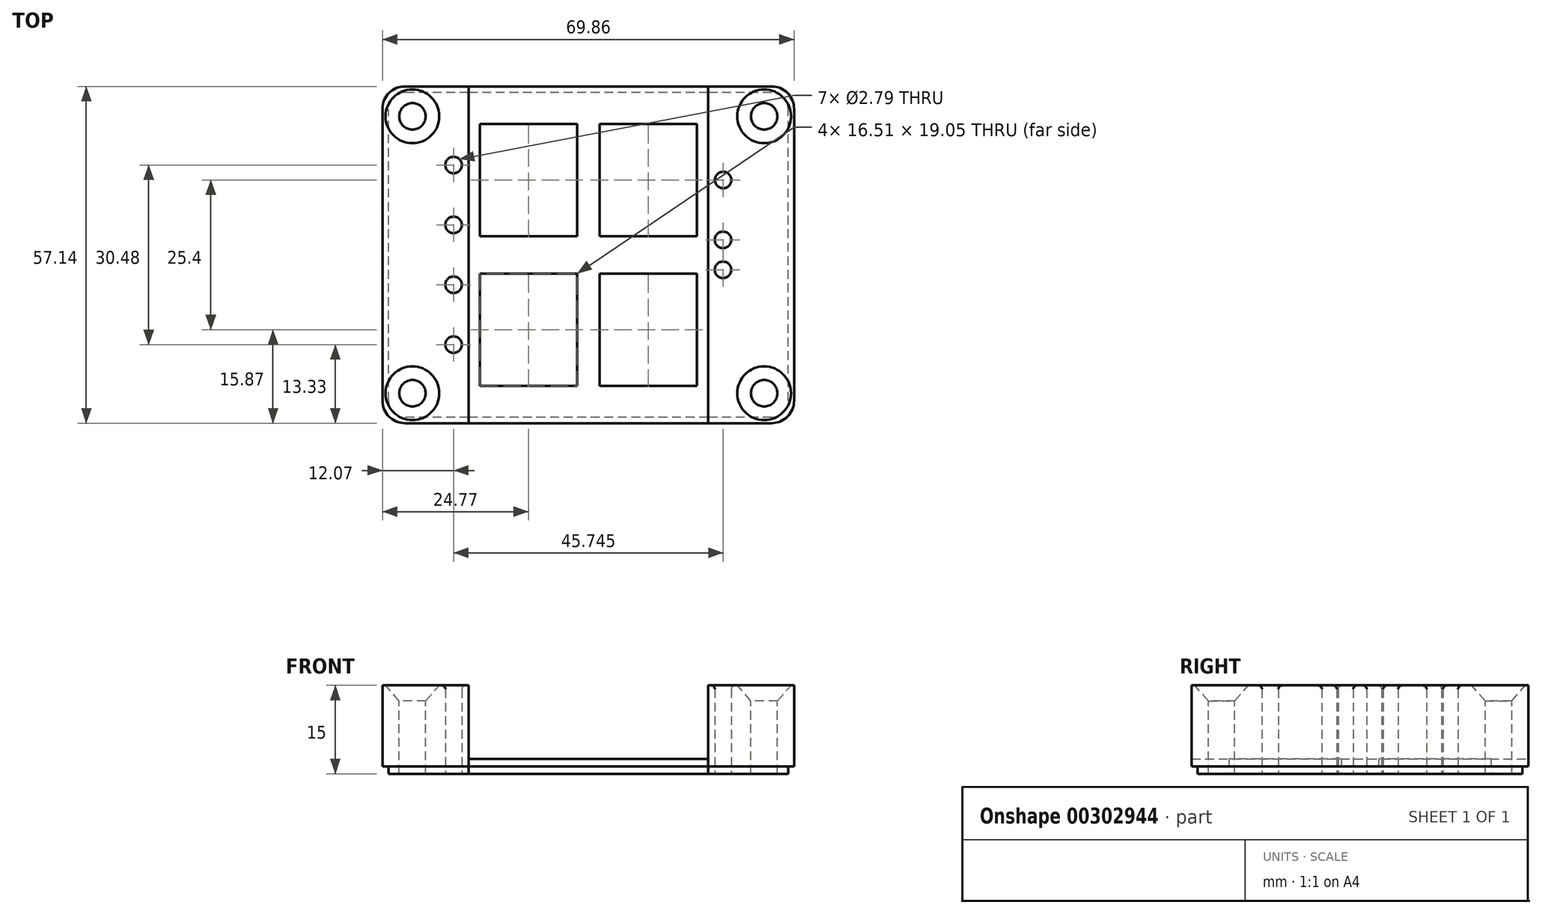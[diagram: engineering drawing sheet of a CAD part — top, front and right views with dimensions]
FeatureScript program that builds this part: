
annotation { "Feature Type Name" : "Feature", "Feature Type Description" : "" }
export const myFeature = defineFeature(function(context is Context, id is Id, definition is map)
    precondition{}
    {
        {
            var Q0;
            Q0=qCreatedBy(makeId("Top.planeOp"),FACE);
            var sketch = newSketch(context, id + "F0", { "sketchPlane" : qUnion([Q0])});
            skLineSegment(sketch, "E0.bottom", {"start": v(34.93, -28.58) * mm, "end": v(-34.93, -28.58) * mm});
            skLineSegment(sketch, "E0.top", {"start": v(34.93, 28.58) * mm, "end": v(-34.93, 28.57) * mm});
            skLineSegment(sketch, "E0.left", {"start": v(34.93, -28.58) * mm, "end": v(34.93, 28.58) * mm});
            skLineSegment(sketch, "E0.right", {"start": v(-34.93, -28.58) * mm, "end": v(-34.93, 28.58) * mm});
            skPoint(sketch, "E0.middle", {"position": v(0, 0) * mm});
            skLineSegment(sketch, "E1.bottom", {"start": v(20.32, -25.65) * mm, "end": v(-20.32, -25.65) * mm});
            skLineSegment(sketch, "E1.top", {"start": v(20.32, 25.65) * mm, "end": v(-20.32, 25.65) * mm});
            skLineSegment(sketch, "E1.left", {"start": v(20.32, -25.65) * mm, "end": v(20.32, 25.65) * mm});
            skLineSegment(sketch, "E1.right", {"start": v(-20.32, -25.65) * mm, "end": v(-20.32, 25.65) * mm});
            skCircle(sketch, "E2", {"center": v(-22.86, -15.24) * mm, "radius": 1.4 * mm});
            skCircle(sketch, "E3", {"center": v(-22.86, -5.08) * mm, "radius": 1.4 * mm});
            skCircle(sketch, "E4", {"center": v(-22.86, 5.08) * mm, "radius": 1.4 * mm});
            skCircle(sketch, "E5", {"center": v(-22.86, 15.24) * mm, "radius": 1.4 * mm});
            skCircle(sketch, "E6", {"center": v(22.86, -2.54) * mm, "radius": 1.4 * mm});
            skCircle(sketch, "E7", {"center": v(22.86, 2.54) * mm, "radius": 1.4 * mm});
            skCircle(sketch, "E8", {"center": v(22.88, 12.7) * mm, "radius": 1.4 * mm});
            skLineSegment(sketch, "E9", {"start": v(-20.32, -25.65) * mm, "end": v(-20.32, -28.58) * mm});
            skLineSegment(sketch, "E10", {"start": v(20.32, -25.65) * mm, "end": v(20.32, -28.58) * mm});
            skLineSegment(sketch, "E11", {"start": v(20.32, 25.65) * mm, "end": v(20.32, 28.58) * mm});
            skLineSegment(sketch, "E12", {"start": v(-20.32, 25.65) * mm, "end": v(-20.32, 28.57) * mm});
            skLineSegment(sketch, "E13.bottom", {"start": v(1.9, -3.18) * mm, "end": v(18.41, -3.18) * mm});
            skLineSegment(sketch, "E13.top", {"start": v(1.9, -22.23) * mm, "end": v(18.41, -22.23) * mm});
            skLineSegment(sketch, "E13.left", {"start": v(1.9, -3.18) * mm, "end": v(1.9, -22.23) * mm});
            skLineSegment(sketch, "E13.right", {"start": v(18.41, -3.18) * mm, "end": v(18.41, -22.23) * mm});
            skPoint(sketch, "E13.middle", {"position": v(10.16, -12.7) * mm});
            skLineSegment(sketch, "E14.0.1.0", {"start": v(18.41, 22.22) * mm, "end": v(18.41, 3.17) * mm});
            skLineSegment(sketch, "E14.0.1.1", {"start": v(1.9, 22.22) * mm, "end": v(1.9, 3.17) * mm});
            skLineSegment(sketch, "E14.0.1.2", {"start": v(1.9, 3.17) * mm, "end": v(18.41, 3.17) * mm});
            skLineSegment(sketch, "E14.0.1.3", {"start": v(1.9, 22.22) * mm, "end": v(18.41, 22.22) * mm});
            skLineSegment(sketch, "E14.1.0.0", {"start": v(-1.9, -3.18) * mm, "end": v(-1.9, -22.23) * mm});
            skLineSegment(sketch, "E14.1.0.1", {"start": v(-18.42, -3.18) * mm, "end": v(-18.42, -22.23) * mm});
            skLineSegment(sketch, "E14.1.0.2", {"start": v(-18.42, -22.23) * mm, "end": v(-1.9, -22.23) * mm});
            skLineSegment(sketch, "E14.1.0.3", {"start": v(-18.42, -3.18) * mm, "end": v(-1.9, -3.18) * mm});
            skLineSegment(sketch, "E14.1.1.0", {"start": v(-1.9, 22.22) * mm, "end": v(-1.9, 3.17) * mm});
            skLineSegment(sketch, "E14.1.1.1", {"start": v(-18.42, 22.22) * mm, "end": v(-18.42, 3.17) * mm});
            skLineSegment(sketch, "E14.1.1.2", {"start": v(-18.42, 3.17) * mm, "end": v(-1.9, 3.17) * mm});
            skLineSegment(sketch, "E14.1.1.3", {"start": v(-18.42, 22.22) * mm, "end": v(-1.9, 22.22) * mm});
            skLineSegment(sketch, "E14.direction1", {"start": v(1.9, -3.18) * mm, "end": v(-18.42, -3.18) * mm, "construction": true});
            skLineSegment(sketch, "E14.direction2", {"start": v(1.9, -3.18) * mm, "end": v(1.9, 22.22) * mm, "construction": true});
            skSolve(sketch);
        }
        {
            var Q0;
            {var subQ0=sQuery(id+"F0.wireOp",EDGE,"E0.right");Q0=makeQuery(id+"F0.imprint","IMPRINT",FACE,{"disambiguationData":[TD([[makeQuery(id+"F0.imprint","IMPRINT",EDGE,{"derivedFrom":subQ0}),-1.0]])]});}
            var Q1;
            {var subQ1=sQuery(id+"F0.wireOp",EDGE,"E0.left");Q1=makeQuery(id+"F0.imprint","IMPRINT",FACE,{"disambiguationData":[TD([[makeQuery(id+"F0.imprint","IMPRINT",EDGE,{"derivedFrom":subQ1}),1.0]])]});}
            var Q2;
            Q2=makeQuery(id+"F0.imprint","IMPRINT",FACE,{"disambiguationData":[TD([[makeQuery(id+"F0.imprint","IMPRINT",EDGE,{"derivedFrom":sQuery(id+"F0.wireOp",EDGE,"b5f2c712-6844-453f-bde0-8a3109862096")}),1.0]])]});
            var Q3;
            Q3=makeQuery(id+"F0.imprint","IMPRINT",FACE,{"disambiguationData":[TD([[makeQuery(id+"F0.imprint","IMPRINT",EDGE,{"derivedFrom":sQuery(id+"F0.wireOp",EDGE,"b4171f42-6c98-4037-92a8-ff7a6a93fe7b")}),1.0]])]});
            var Q4;
            Q4=makeQuery(id+"F0.imprint","IMPRINT",FACE,{"disambiguationData":[TD([[makeQuery(id+"F0.imprint","IMPRINT",EDGE,{"derivedFrom":sQuery(id+"F0.wireOp",EDGE,"d604e2b2-1cbf-4e45-8d46-6f62e81bd806")}),1.0]])]});
            var Q5;
            Q5=makeQuery(id+"F0.imprint","IMPRINT",FACE,{"disambiguationData":[TD([[makeQuery(id+"F0.imprint","IMPRINT",EDGE,{"derivedFrom":sQuery(id+"F0.wireOp",EDGE,"b88a7e70-b00d-4436-bc84-b71cc6af67d6")}),1.0]])]});
            extrude(context, id + "F1", {"entities" : qUnion([Q0, Q1, Q2, Q3, Q4, Q5]), "depth" : 15 * mm});
        }
        {
            var Q0;
            Q0=makeQuery(id+"F0.imprint","IMPRINT",FACE,{"disambiguationData":[TD([[makeQuery(id+"F0.imprint","IMPRINT",EDGE,{"derivedFrom":sQuery(id+"F0.wireOp",EDGE,"E1.bottom")}),-1.0]])]});
            var Q1;
            Q1=makeQuery(id+"F0.imprint","IMPRINT",FACE,{"disambiguationData":[TD([[makeQuery(id+"F0.imprint","IMPRINT",EDGE,{"derivedFrom":sQuery(id+"F0.wireOp",EDGE,"E1.bottom")}),1.0]])]});
            var Q2;
            Q2=makeQuery(id+"F0.imprint","IMPRINT",FACE,{"disambiguationData":[TD([[makeQuery(id+"F0.imprint","IMPRINT",EDGE,{"derivedFrom":sQuery(id+"F0.wireOp",EDGE,"E1.top")}),-1.0]])]});
            extrude(context, id + "F2", {"entities" : qUnion([Q0, Q1, Q2]), "depth" : 2.54 * mm});
        }
        {
            var Q0;
            Q0=makeQuery(id+"F1.opExtrude","SWEPT_EDGE",EDGE,{"disambiguationData":[OSD([sQuery(id+"F0.wireOp",EDGE,"E0.bottom"),sQuery(id+"F0.wireOp",EDGE,"E0.left")])]});
            var Q1;
            Q1=makeQuery(id+"F1.opExtrude","SWEPT_EDGE",EDGE,{"disambiguationData":[OSD([sQuery(id+"F0.wireOp",EDGE,"E0.bottom"),sQuery(id+"F0.wireOp",EDGE,"E0.right")])]});
            var Q2;
            Q2=makeQuery(id+"F1.opExtrude","SWEPT_EDGE",EDGE,{"disambiguationData":[OSD([sQuery(id+"F0.wireOp",EDGE,"E0.top"),sQuery(id+"F0.wireOp",EDGE,"E0.left")])]});
            var Q3;
            Q3=makeQuery(id+"F1.opExtrude","SWEPT_EDGE",EDGE,{"disambiguationData":[OSD([sQuery(id+"F0.wireOp",EDGE,"E0.top"),sQuery(id+"F0.wireOp",EDGE,"E0.right")])]});
            fillet(context, id + "F3", {"entities" : qUnion([Q0, Q1, Q2, Q3]), "radius" : 3.8 * mm, "tangentPropagation" : true, "allowEdgeOverflow" : false});
        }
        {
            var Q0;
            Q0=makeQuery(id+"F1.opExtrude","CAP_EDGE",EDGE,{"disambiguationData":[OSD([sQuery(id+"F0.wireOp",EDGE,"E2")])],"isStart":false});
            var Q1;
            Q1=makeQuery(id+"F1.opExtrude","CAP_EDGE",EDGE,{"disambiguationData":[OSD([sQuery(id+"F0.wireOp",EDGE,"E3")])],"isStart":false});
            var Q2;
            Q2=makeQuery(id+"F1.opExtrude","CAP_EDGE",EDGE,{"disambiguationData":[OSD([sQuery(id+"F0.wireOp",EDGE,"E4")])],"isStart":false});
            var Q3;
            Q3=makeQuery(id+"F1.opExtrude","CAP_EDGE",EDGE,{"disambiguationData":[OSD([sQuery(id+"F0.wireOp",EDGE,"E5")])],"isStart":false});
            var Q4;
            Q4=makeQuery(id+"F1.opExtrude","CAP_EDGE",EDGE,{"disambiguationData":[OSD([sQuery(id+"F0.wireOp",EDGE,"E8")])],"isStart":false});
            var Q5;
            Q5=makeQuery(id+"F1.opExtrude","CAP_EDGE",EDGE,{"disambiguationData":[OSD([sQuery(id+"F0.wireOp",EDGE,"E7")])],"isStart":false});
            var Q6;
            Q6=makeQuery(id+"F1.opExtrude","CAP_EDGE",EDGE,{"disambiguationData":[OSD([sQuery(id+"F0.wireOp",EDGE,"E6")])],"isStart":false});
            fillet(context, id + "F4", {"entities" : qUnion([Q0, Q1, Q2, Q3, Q4, Q5, Q6]), "radius" : 0.64 * mm, "tangentPropagation" : true, "allowEdgeOverflow" : false});
        }
        {
            var Q0;
            Q0=qCreatedBy(makeId("Top.planeOp"),FACE);
            cPlane(context, id + "F5", {"entities" : qUnion([Q0]), "cplaneType" : CPlaneType.OFFSET, "offset" : 15 * mm, "width" : 152.4 * mm, "height" : 152.4 * mm});
        }
        {
            var Q0;
            Q0=qCreatedBy(id+"F5.planeOp",FACE);
            var sketch = newSketch(context, id + "F6", { "sketchPlane" : qUnion([Q0])});
            skPoint(sketch, "E15", {"position": v(29.85, -23.5) * mm});
            skPoint(sketch, "E16", {"position": v(29.85, 23.5) * mm});
            skPoint(sketch, "E17", {"position": v(-29.85, 23.5) * mm});
            skPoint(sketch, "E18", {"position": v(-29.85, -23.5) * mm});
            skSolve(sketch);
        }
        {
            var Q0;
            Q0=sQuery(id+"F6.wireOp",VERTEX,"E15");
            var Q1;
            Q1=sQuery(id+"F6.wireOp",VERTEX,"E16");
            var Q2;
            Q2=sQuery(id+"F6.wireOp",VERTEX,"E17");
            var Q3;
            Q3=sQuery(id+"F6.wireOp",VERTEX,"E18");
            var Q4;
            Q4=makeQuery(id+"F1.opExtrude","SWEPT_BODY",BODY,{"disambiguationData":[OSD([sQuery(id+"F0.wireOp",EDGE,"E0.bottom"),sQuery(id+"F0.wireOp",EDGE,"E0.top"),sQuery(id+"F0.wireOp",EDGE,"E0.left"),sQuery(id+"F0.wireOp",EDGE,"E1.left"),sQuery(id+"F0.wireOp",EDGE,"E6"),sQuery(id+"F0.wireOp",EDGE,"E7"),sQuery(id+"F0.wireOp",EDGE,"E8"),sQuery(id+"F0.wireOp",EDGE,"E10"),sQuery(id+"F0.wireOp",EDGE,"E11")])]});
            var Q5;
            Q5=makeQuery(id+"F1.opExtrude","SWEPT_BODY",BODY,{"disambiguationData":[OSD([sQuery(id+"F0.wireOp",EDGE,"E0.bottom"),sQuery(id+"F0.wireOp",EDGE,"E0.top"),sQuery(id+"F0.wireOp",EDGE,"E0.right"),sQuery(id+"F0.wireOp",EDGE,"E1.right"),sQuery(id+"F0.wireOp",EDGE,"E2"),sQuery(id+"F0.wireOp",EDGE,"E3"),sQuery(id+"F0.wireOp",EDGE,"E4"),sQuery(id+"F0.wireOp",EDGE,"E5"),sQuery(id+"F0.wireOp",EDGE,"E9"),sQuery(id+"F0.wireOp",EDGE,"E12")])]});
            hole(context, id + "F7", {"style" : HoleStyle.C_SINK, "endStyle" : HoleEndStyle.THROUGH, "standardTappedOrClearance" : lookupTablePath({ "standard" : "ANSI", "fit" : "Normal (ASME)", "size" : "#8", "type" : "Clearance" }), "standardBlindInLast" : lookupTablePath({ "fit" : "Free", "standard" : "ANSI", "size" : "#8", "type" : "Clearance" }), "holeDiameter" : 4.5 * mm, "cSinkDiameter" : 9.12 * mm, "cSinkAngle" : 82 * degree, "tappedDepth" : 12.7 * mm, "tapClearance" : 3, "locations" : qUnion([Q0, Q1, Q2, Q3]), "scope" : qUnion([Q4, Q5])});
        }
        {
            var Q0;
            {var subQ0=sQuery(id+"F0.wireOp",EDGE,"E0.left");Q0=makeQuery(id+"F0.imprint","IMPRINT",FACE,{"disambiguationData":[TD([[makeQuery(id+"F0.imprint","IMPRINT",EDGE,{"derivedFrom":subQ0}),1.0]])]});}
            var sketch = newSketch(context, id + "F8", { "sketchPlane" : qUnion([Q0])});
            skLineSegment(sketch, "E19.0", {"start": v(31.12, 27.56) * mm, "end": v(20.32, 27.56) * mm});
            skLineSegment(sketch, "E19.1", {"start": v(20.32, -27.56) * mm, "end": v(-20.32, -27.56) * mm});
            skLineSegment(sketch, "E19.2", {"start": v(31.12, -27.56) * mm, "end": v(20.32, -27.56) * mm});
            skArc(sketch, "E19.3", {"start": v(33.9, -24.77) * mm, "mid": v(33.1, -26.74) * mm, "end": v(31.12, -27.56) * mm});
            skLineSegment(sketch, "E19.4", {"start": v(33.9, -24.77) * mm, "end": v(33.9, 24.77) * mm});
            skLineSegment(sketch, "E19.5", {"start": v(-20.32, -27.56) * mm, "end": v(-31.12, -27.56) * mm});
            skArc(sketch, "E19.6", {"start": v(31.12, 27.56) * mm, "mid": v(33.1, 26.74) * mm, "end": v(33.9, 24.77) * mm});
            skArc(sketch, "E19.7", {"start": v(-31.12, -27.56) * mm, "mid": v(-33.1, -26.74) * mm, "end": v(-33.9, -24.77) * mm});
            skLineSegment(sketch, "E19.8", {"start": v(-33.9, -24.77) * mm, "end": v(-33.9, 24.77) * mm});
            skArc(sketch, "E19.9", {"start": v(-33.9, 24.77) * mm, "mid": v(-33.1, 26.74) * mm, "end": v(-31.12, 27.56) * mm});
            skLineSegment(sketch, "E19.10", {"start": v(-20.32, 27.56) * mm, "end": v(-31.12, 27.56) * mm});
            skLineSegment(sketch, "E19.11", {"start": v(20.32, 27.56) * mm, "end": v(-20.32, 27.56) * mm});
            skArc(sketch, "E20.0", {"start": v(31.12, 28.58) * mm, "mid": v(33.8, 27.46) * mm, "end": v(34.93, 24.77) * mm});
            skLineSegment(sketch, "E20.1", {"start": v(-34.92, -24.77) * mm, "end": v(-34.92, 24.77) * mm});
            skArc(sketch, "E20.2", {"start": v(-34.92, 24.77) * mm, "mid": v(-33.8, 27.46) * mm, "end": v(-31.12, 28.57) * mm});
            skLineSegment(sketch, "E20.3", {"start": v(-20.32, 28.57) * mm, "end": v(-31.12, 28.57) * mm});
            skLineSegment(sketch, "E20.4", {"start": v(20.32, 28.58) * mm, "end": v(-20.32, 28.57) * mm});
            skArc(sketch, "E20.5", {"start": v(-31.12, -28.58) * mm, "mid": v(-33.8, -27.46) * mm, "end": v(-34.92, -24.77) * mm});
            skLineSegment(sketch, "E20.6", {"start": v(31.12, 28.58) * mm, "end": v(20.32, 28.58) * mm});
            skLineSegment(sketch, "E20.7", {"start": v(-20.32, -28.58) * mm, "end": v(-31.12, -28.58) * mm});
            skLineSegment(sketch, "E20.8", {"start": v(20.32, -28.58) * mm, "end": v(-20.32, -28.58) * mm});
            skLineSegment(sketch, "E20.9", {"start": v(31.12, -28.58) * mm, "end": v(20.32, -28.58) * mm});
            skArc(sketch, "E20.10", {"start": v(34.92, -24.77) * mm, "mid": v(33.8, -27.46) * mm, "end": v(31.12, -28.58) * mm});
            skLineSegment(sketch, "E20.11", {"start": v(34.92, -24.77) * mm, "end": v(34.92, 24.77) * mm});
            skSolve(sketch);
        }
        {
            var Q0;
            {var subQ2=sQuery(id+"F8.wireOp",EDGE,"E19.0");Q0=makeQuery(id+"F8.imprint","IMPRINT",FACE,{"disambiguationData":[TD([[makeQuery(id+"F8.imprint","IMPRINT",EDGE,{"derivedFrom":subQ2}),-1.0]])]});}
            var Q1;
            {var subQ3=sQuery(id+"F8.wireOp",EDGE,"E19.1");Q1=makeQuery(id+"F8.imprint","IMPRINT",FACE,{"disambiguationData":[TD([[makeQuery(id+"F8.imprint","IMPRINT",EDGE,{"derivedFrom":subQ3}),1.0]])]});}
            extrude(context, id + "F9", {"entities" : qUnion([Q0, Q1]), "operationType" : NewBodyOperationType.REMOVE, "depth" : 1.27 * mm});
        }
    });
